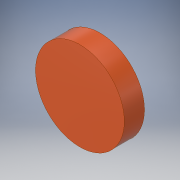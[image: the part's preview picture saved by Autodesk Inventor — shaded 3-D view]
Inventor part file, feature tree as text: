
AUTODESK INVENTOR PART (.ipt)
format: ipt  version: 2019.4 (Build 234330000, 330)  size: 95,232 bytes
history: native  units: in
note: dims shown in document units (in); Inventor stores cm internally (conversion verified against a paired STEP export)
features: extrude x1, sketch x1
ambient origin geometry x8: Origin, YZ Plane, XZ Plane, XY Plane, X Axis, Y Axis, Z Axis, Center Point
bodies: Solid1 (feature_tree)
feature tree (2):
  extrude  "Extrusion1"  Depth=0.125in TaperAngle=0.0deg
  sketch  "Sketch1"  dims[d0=0.55in d1=0.125in d2=0.0in]
